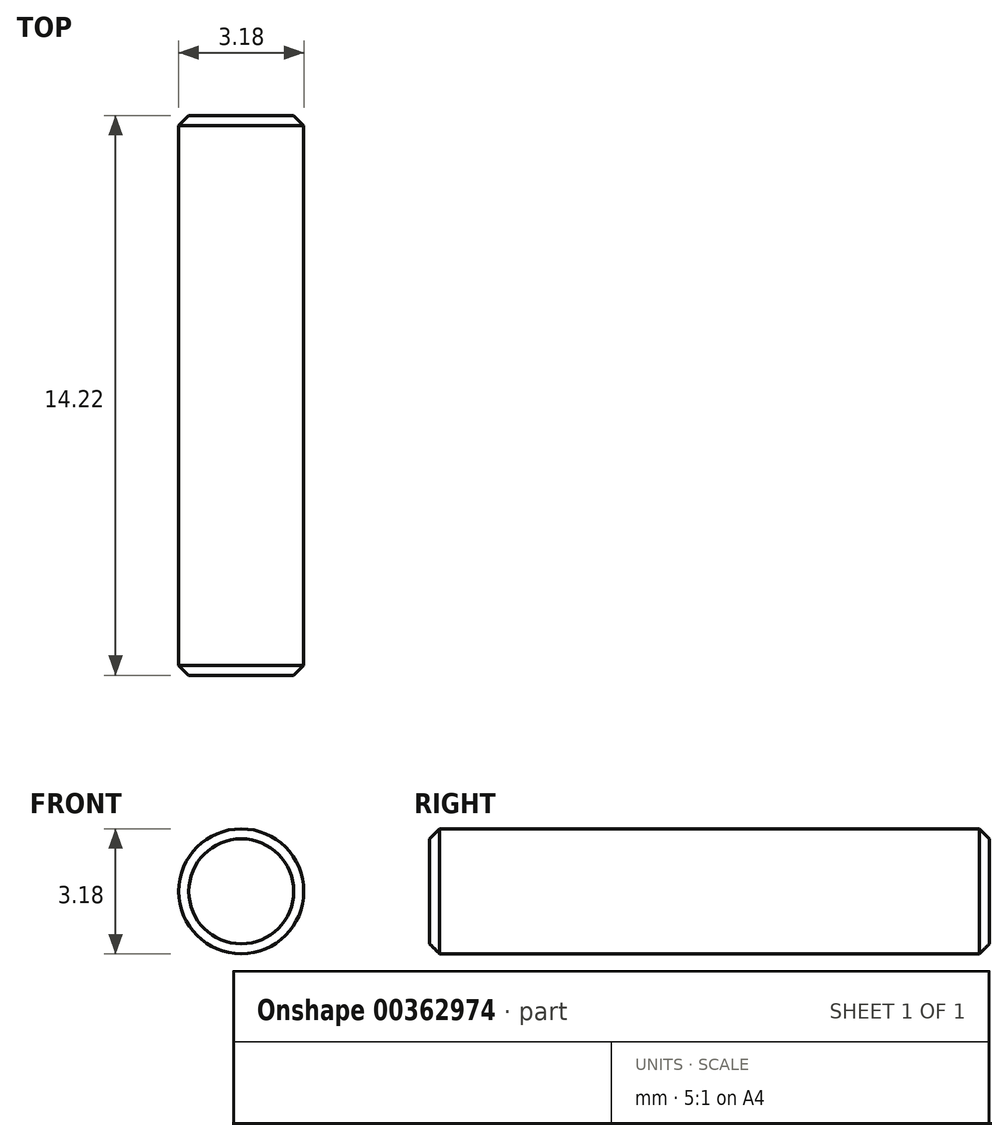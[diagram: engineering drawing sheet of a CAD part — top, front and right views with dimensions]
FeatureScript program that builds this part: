
annotation { "Feature Type Name" : "Feature", "Feature Type Description" : "" }
export const myFeature = defineFeature(function(context is Context, id is Id, definition is map)
    precondition{}
    {
        {
            var Q0;
            Q0=qCreatedBy(makeId("Front.planeOp"),FACE);
            var sketch = newSketch(context, id + "F0", { "sketchPlane" : qUnion([Q0])});
            skCircle(sketch, "E0", {"center": v(0, 0) * mm, "radius": 1.59 * mm});
            skSolve(sketch);
        }
        {
            var Q0;
            Q0=makeQuery(id+"F0.imprint","IMPRINT",FACE,{"disambiguationData":[TD([[makeQuery(id+"F0.imprint","IMPRINT",EDGE,{"derivedFrom":sQuery(id+"F0.wireOp",EDGE,"E0")}),1.0]])]});
            extrude(context, id + "F1", {"entities" : qUnion([Q0]), "depth" : 14.22 * mm});
        }
        {
            var Q0;
            Q0=makeQuery(id+"F1.opExtrude","CAP_EDGE",EDGE,{"disambiguationData":[OSD([sQuery(id+"F0.wireOp",EDGE,"E0")])],"isStart":false});
            var Q1;
            Q1=makeQuery(id+"F1.opExtrude","CAP_EDGE",EDGE,{"disambiguationData":[OSD([sQuery(id+"F0.wireOp",EDGE,"E0")])],"isStart":true});
            chamfer(context, id + "F2", {"entities" : qUnion([Q0, Q1]), "chamferType" : ChamferType.OFFSET_ANGLE, "width" : 0.25 * mm, "oppositeDirection" : false, "angle" : 45 * degree, "tangentPropagation" : true});
        }
    });
